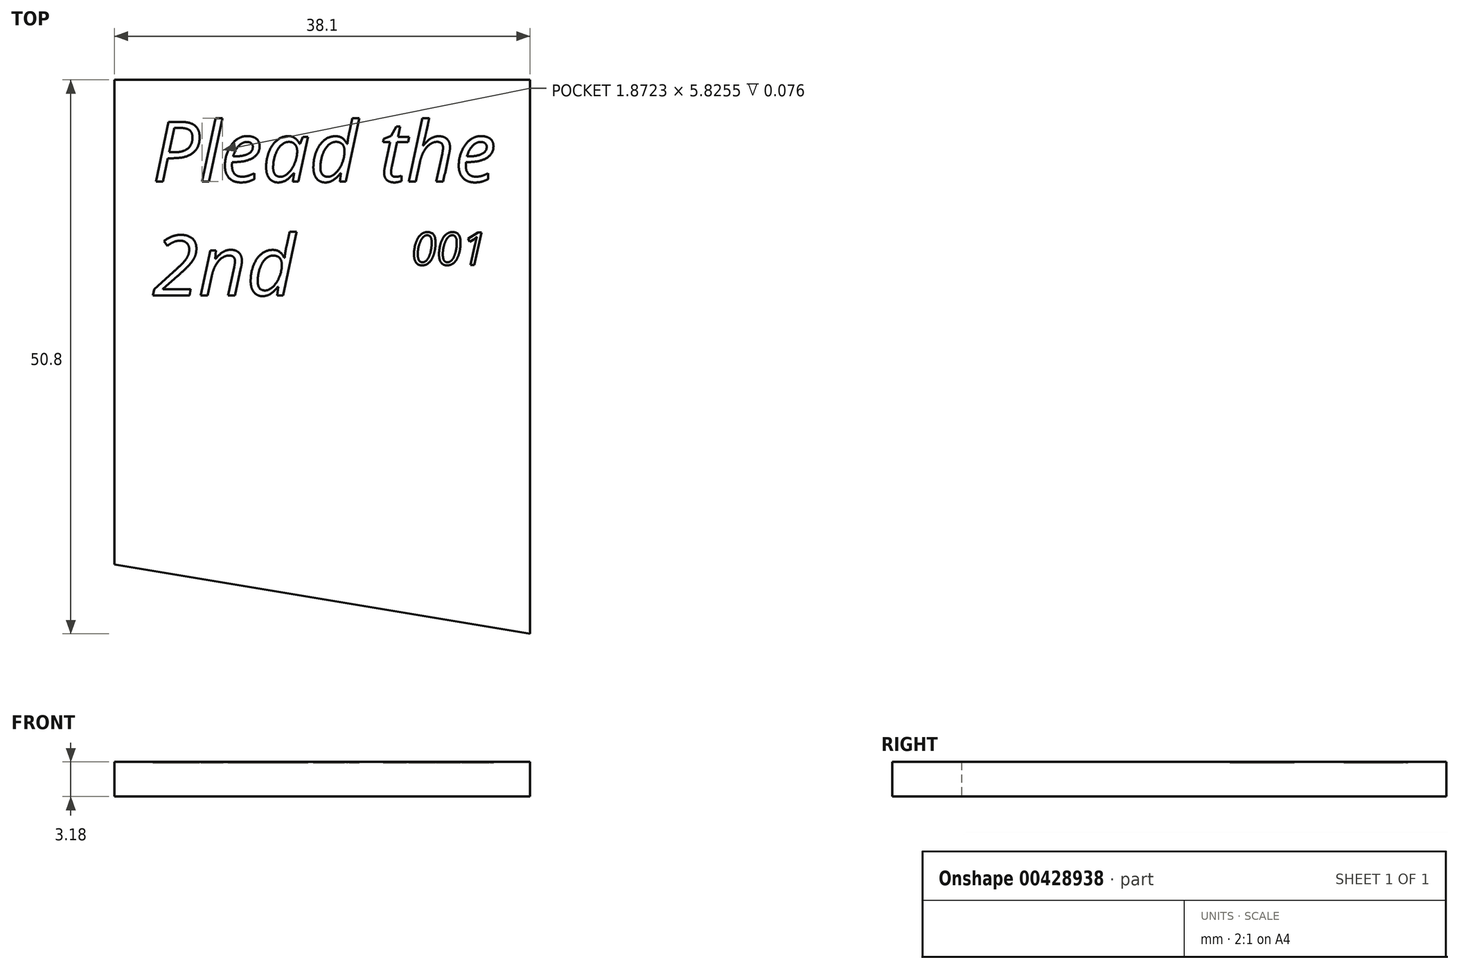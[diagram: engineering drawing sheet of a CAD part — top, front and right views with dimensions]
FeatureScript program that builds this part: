
annotation { "Feature Type Name" : "Feature", "Feature Type Description" : "" }
export const myFeature = defineFeature(function(context is Context, id is Id, definition is map)
    precondition{}
    {
        {
            var Q0;
            Q0=qCreatedBy(makeId("Top.planeOp"),FACE);
            var sketch = newSketch(context, id + "F0", { "sketchPlane" : qUnion([Q0])});
            skLineSegment(sketch, "E0.bottom", {"start": v(-19.05, 25.4) * mm, "end": v(19.05, 25.4) * mm});
            skLineSegment(sketch, "E0.right", {"start": v(19.05, 25.4) * mm, "end": v(19.05, -25.4) * mm});
            skPoint(sketch, "E0.middle", {"position": v(0, 0) * mm});
            skLineSegment(sketch, "E1", {"start": v(-19.05, 25.4) * mm, "end": v(-19.05, -19.05) * mm});
            skLineSegment(sketch, "E2", {"start": v(-19.05, -19.05) * mm, "end": v(19.05, -25.4) * mm});
            skSolve(sketch);
        }
        {
            var Q0;
            Q0 = qSketchRegion(id + "F0", true);
            extrude(context, id + "F1", {"entities" : qUnion([Q0]), "depth" : 3.17 * mm});
        }
        {
            var Q0;
            Q0=makeQuery(id+"F1.opExtrude","CAP_FACE",FACE,{"disambiguationData":[OSD([sQuery(id+"F0.wireOp",EDGE,"E0.bottom"),sQuery(id+"F0.wireOp",EDGE,"E0.right"),sQuery(id+"F0.wireOp",EDGE,"E1"),sQuery(id+"F0.wireOp",EDGE,"E2")])],"isStart":false});
            var sketch = newSketch(context, id + "F2", { "sketchPlane" : qUnion([Q0])});
            skText(sketch, "E3", { "text": "Plead the\n2nd", "fontName": "OpenSans-Italic.ttf"});
            const initialGuessF2  = {"E3": [-0.01557, 0.01606, 1, 0, 0.00552]};
            skSetInitialGuess(sketch, initialGuessF2);
            skSolve(sketch);
        }
        {
            var Q0;
            Q0 = qSketchRegion(id + "F2", true);
            extrude(context, id + "F3", {"entities" : qUnion([Q0]), "operationType" : NewBodyOperationType.REMOVE, "oppositeDirection" : true, "depth" : 0.08 * mm});
        }
        {
            var Q0;
            {var subQ0=sQuery(id+"F0.wireOp",EDGE,"E0.right");var subQ1=sQuery(id+"F0.wireOp",EDGE,"E2");var subQ2=sQuery(id+"F0.wireOp",EDGE,"E0.bottom");var subQ3=sQuery(id+"F0.wireOp",EDGE,"E1");Q0=makeQuery(id+"F3.boolean.opBoolean","SPLIT",FACE,{"disambiguationData":[TD([makeQuery(id+"F1.opExtrude","SWEPT_FACE",FACE,{"disambiguationData":[OSD([subQ2])]})])],"derivedFrom":makeQuery(id+"F1.opExtrude","CAP_FACE",FACE,{"disambiguationData":[OSD([subQ2,subQ0,subQ3,subQ1])],"isStart":false})});}
            var sketch = newSketch(context, id + "F4", { "sketchPlane" : qUnion([Q0])});
            skText(sketch, "E4", { "text": "001", "fontName": "OpenSans-Italic.ttf"});
            const initialGuessF4  = {"E4": [0.00817, 0.00842, 1, 0, 0.003]};
            skSetInitialGuess(sketch, initialGuessF4);
            skSolve(sketch);
        }
        {
            var Q0;
            Q0 = qSketchRegion(id + "F4", true);
            extrude(context, id + "F5", {"entities" : qUnion([Q0]), "operationType" : NewBodyOperationType.REMOVE, "oppositeDirection" : true, "depth" : 0.08 * mm});
        }
    });
